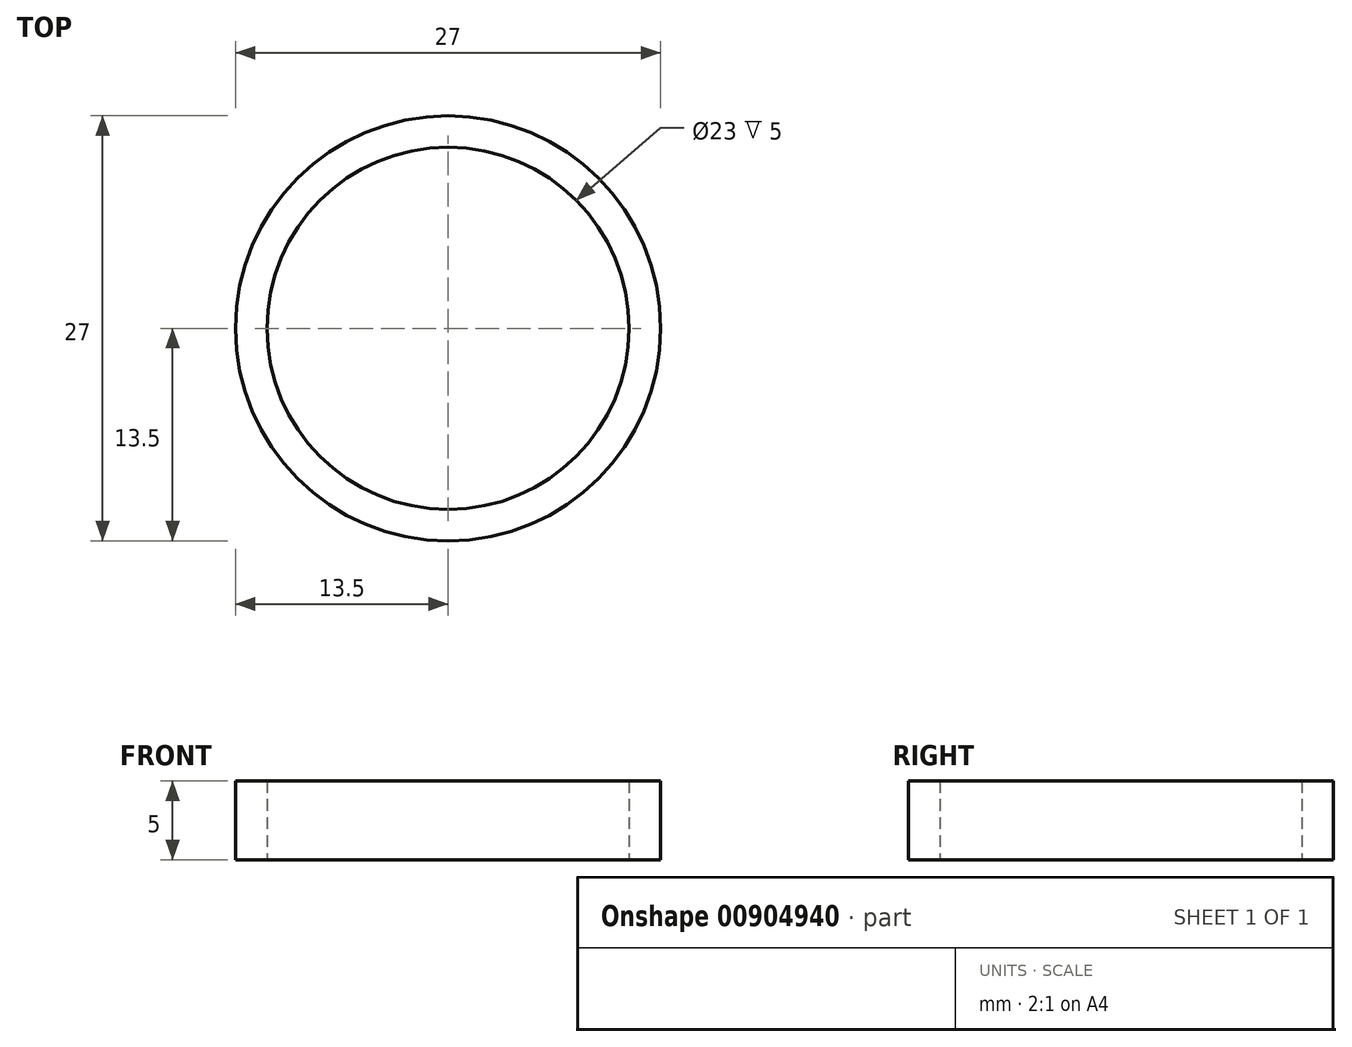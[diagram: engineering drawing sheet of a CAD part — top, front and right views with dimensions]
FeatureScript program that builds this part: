
annotation { "Feature Type Name" : "Feature", "Feature Type Description" : "" }
export const myFeature = defineFeature(function(context is Context, id is Id, definition is map)
    precondition{}
    {
        {
            var Q0;
            Q0=qCreatedBy(makeId("Top.planeOp"),FACE);
            var sketch = newSketch(context, id + "F0", { "sketchPlane" : qUnion([Q0])});
            skCircle(sketch, "E0", {"center": v(0, 0) * mm, "radius": 11.5 * mm});
            skCircle(sketch, "E1", {"center": v(0, 0) * mm, "radius": 13.5 * mm});
            skSolve(sketch);
        }
        {
            var Q0;
            Q0=qSketchRegion(id+"F0",true);
            extrude(context, id + "F1", {"entities" : qUnion([Q0]), "depth" : 5 * mm, "offsetDistance" : 25 * mm});
        }
    });
